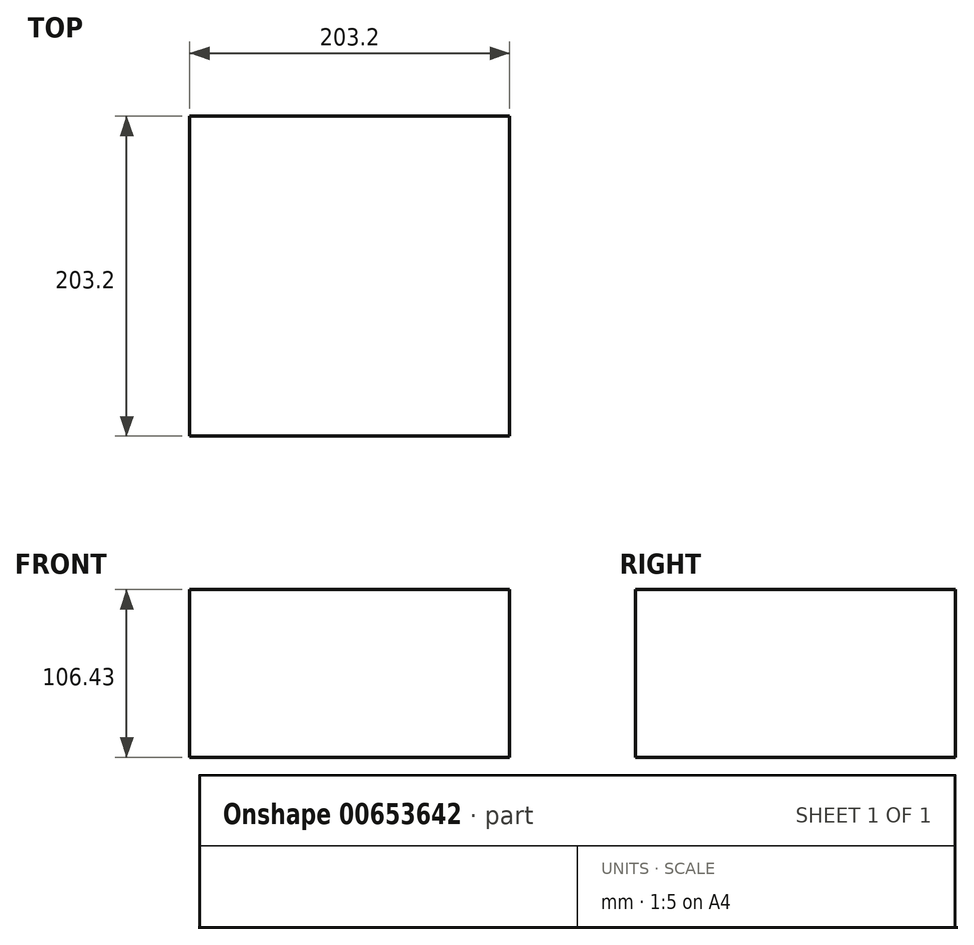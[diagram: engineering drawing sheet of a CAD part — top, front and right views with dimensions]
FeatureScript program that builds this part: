
annotation { "Feature Type Name" : "Feature", "Feature Type Description" : "" }
export const myFeature = defineFeature(function(context is Context, id is Id, definition is map)
    precondition{}
    {
        {
            var Q0;
            Q0=qCreatedBy(makeId("Top.planeOp"),FACE);
            var sketch = newSketch(context, id + "F0", { "sketchPlane" : qUnion([Q0])});
            skLineSegment(sketch, "E0.bottom", {"start": v(101.6, 101.6) * mm, "end": v(-101.6, 101.6) * mm});
            skLineSegment(sketch, "E0.top", {"start": v(101.6, -101.6) * mm, "end": v(-101.6, -101.6) * mm});
            skLineSegment(sketch, "E0.left", {"start": v(101.6, 101.6) * mm, "end": v(101.6, -101.6) * mm});
            skLineSegment(sketch, "E0.right", {"start": v(-101.6, 101.6) * mm, "end": v(-101.6, -101.6) * mm});
            skPoint(sketch, "E0.middle", {"position": v(0, 0) * mm});
            skSolve(sketch);
        }
        {
            var Q0;
            Q0=makeQuery(id+"F0.imprint","IMPRINT",FACE,{"disambiguationData":[TD([[makeQuery(id+"F0.imprint","IMPRINT",EDGE,{"derivedFrom":sQuery(id+"F0.wireOp",EDGE,"E0.bottom")}),1.0]])]});
            extrude(context, id + "F1", {"entities" : qUnion([Q0]), "oppositeDirection" : true, "depth" : 106.43 * mm, "offsetDistance" : 25.4 * mm});
        }
    });
